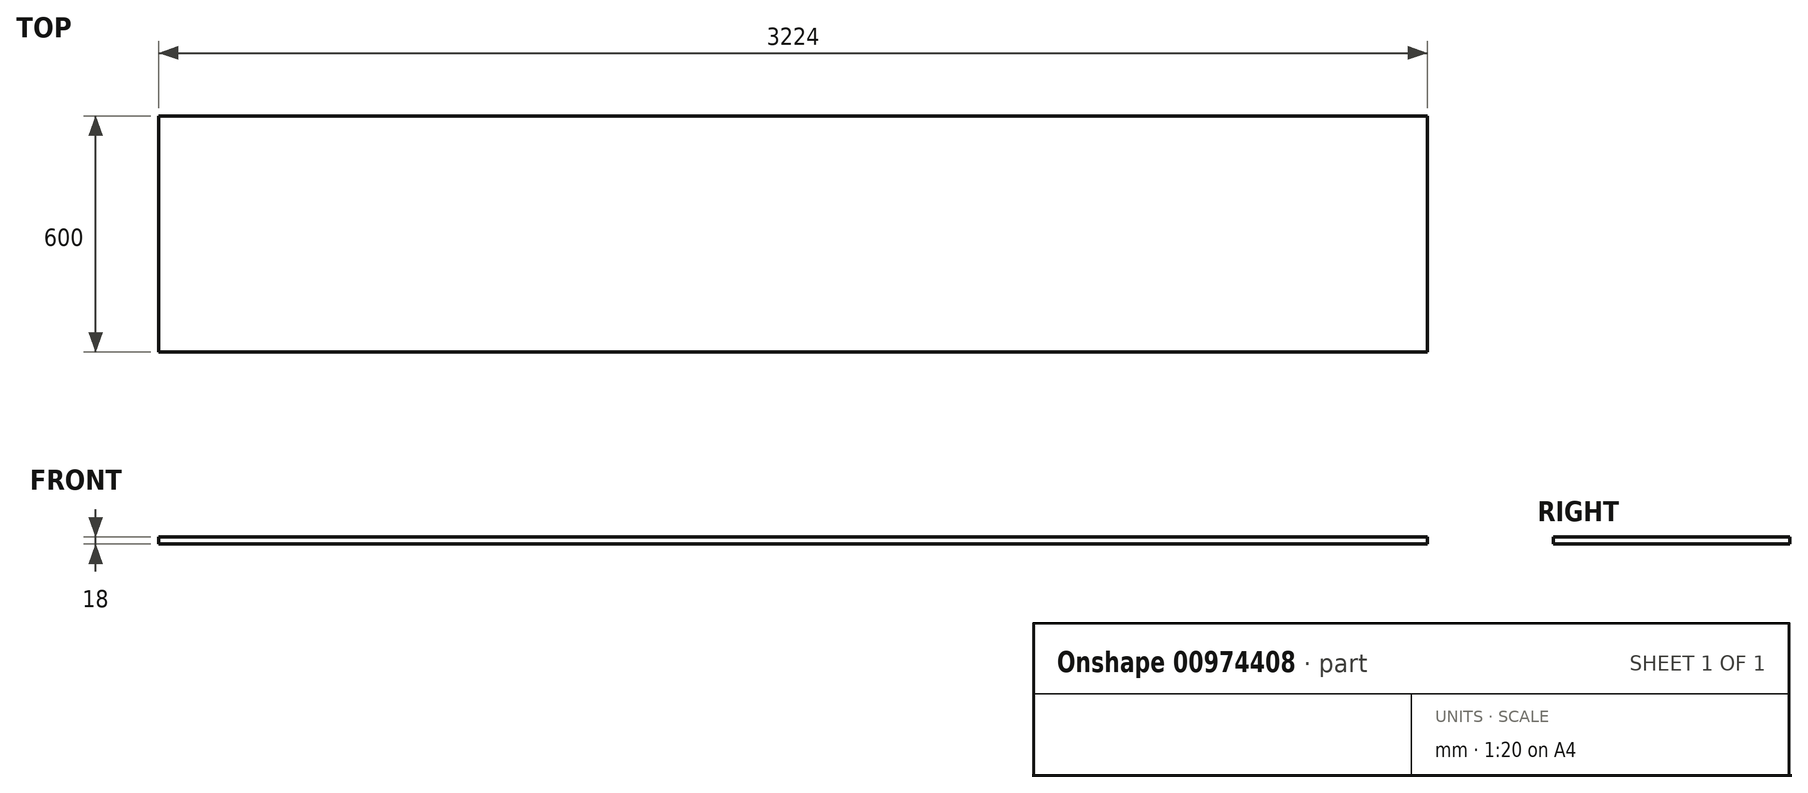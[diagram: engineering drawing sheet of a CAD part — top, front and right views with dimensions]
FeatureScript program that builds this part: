
annotation { "Feature Type Name" : "Feature", "Feature Type Description" : "" }
export const myFeature = defineFeature(function(context is Context, id is Id, definition is map)
    precondition{}
    {
        {
            var Q0;
            Q0=qCreatedBy(makeId("Top.planeOp"),FACE);
            var sketch = newSketch(context, id + "F0", { "sketchPlane" : qUnion([Q0])});
            skLineSegment(sketch, "E0.bottom", {"start": v(1612, 300) * mm, "end": v(-1612, 300) * mm});
            skLineSegment(sketch, "E0.top", {"start": v(1612, -300) * mm, "end": v(-1612, -300) * mm});
            skLineSegment(sketch, "E0.left", {"start": v(1612, 300) * mm, "end": v(1612, -300) * mm});
            skLineSegment(sketch, "E0.right", {"start": v(-1612, 300) * mm, "end": v(-1612, -300) * mm});
            skPoint(sketch, "E0.middle", {"position": v(0, 0) * mm});
            skSolve(sketch);
        }
        {
            var Q0;
            Q0=makeQuery(id+"F0.imprint","IMPRINT",FACE,{"disambiguationData":[TD([[makeQuery(id+"F0.imprint","IMPRINT",EDGE,{"derivedFrom":sQuery(id+"F0.wireOp",EDGE,"E0.bottom")}),1.0]])]});
            extrude(context, id + "F1", {"entities" : qUnion([Q0]), "depth" : 18 * mm, "offsetDistance" : 25 * mm});
        }
    });
